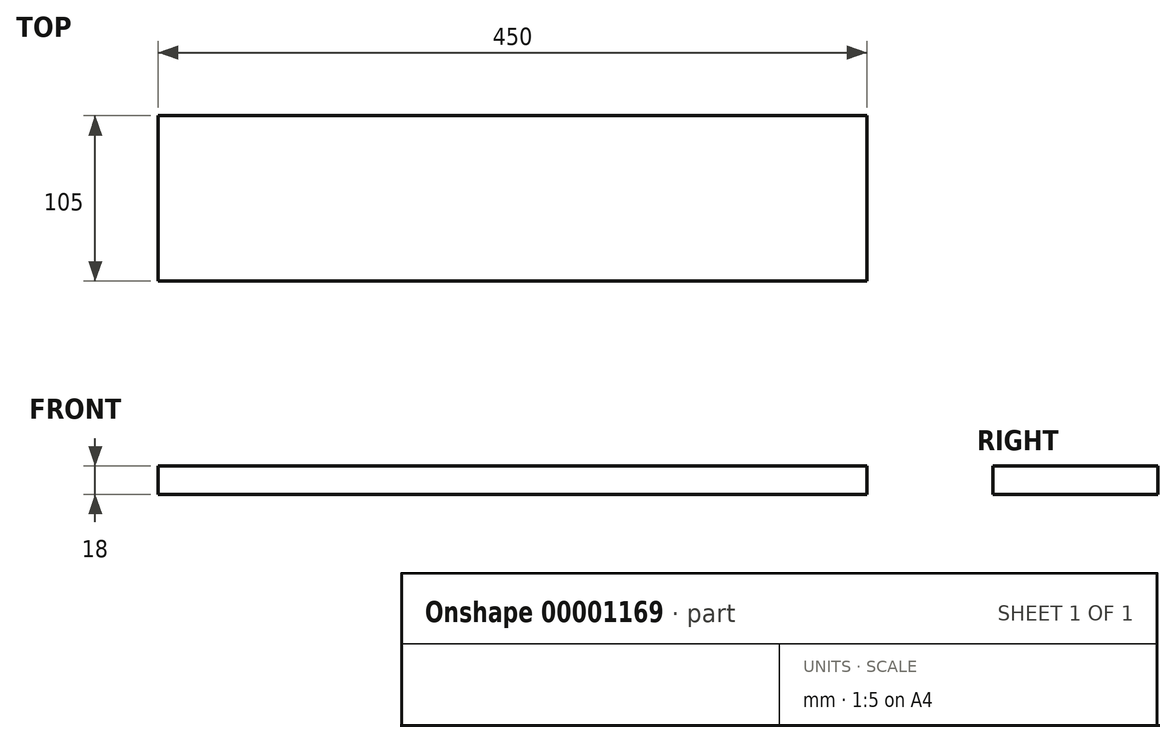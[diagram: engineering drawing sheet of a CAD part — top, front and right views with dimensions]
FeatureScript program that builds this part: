
annotation { "Feature Type Name" : "Feature", "Feature Type Description" : "" }
export const myFeature = defineFeature(function(context is Context, id is Id, definition is map)
    precondition{}
    {
        {
            var Q0;
            Q0=qCreatedBy(makeId("Top.planeOp"),FACE);
            var sketch = newSketch(context, id + "F0", { "sketchPlane" : qUnion([Q0])});
            skLineSegment(sketch, "E0.bottom", {"start": v(0, 0) * mm, "end": v(450, 0) * mm});
            skLineSegment(sketch, "E0.top", {"start": v(0, 105) * mm, "end": v(450, 105) * mm});
            skLineSegment(sketch, "E0.left", {"start": v(0, 0) * mm, "end": v(0, 105) * mm});
            skLineSegment(sketch, "E0.right", {"start": v(450, 0) * mm, "end": v(450, 105) * mm});
            skSolve(sketch);
        }
        {
            var Q0;
            Q0 = qSketchRegion(id + "F0", true);
            extrude(context, id + "F1", {"entities" : qUnion([Q0]), "depth" : 18 * mm});
        }
    });
